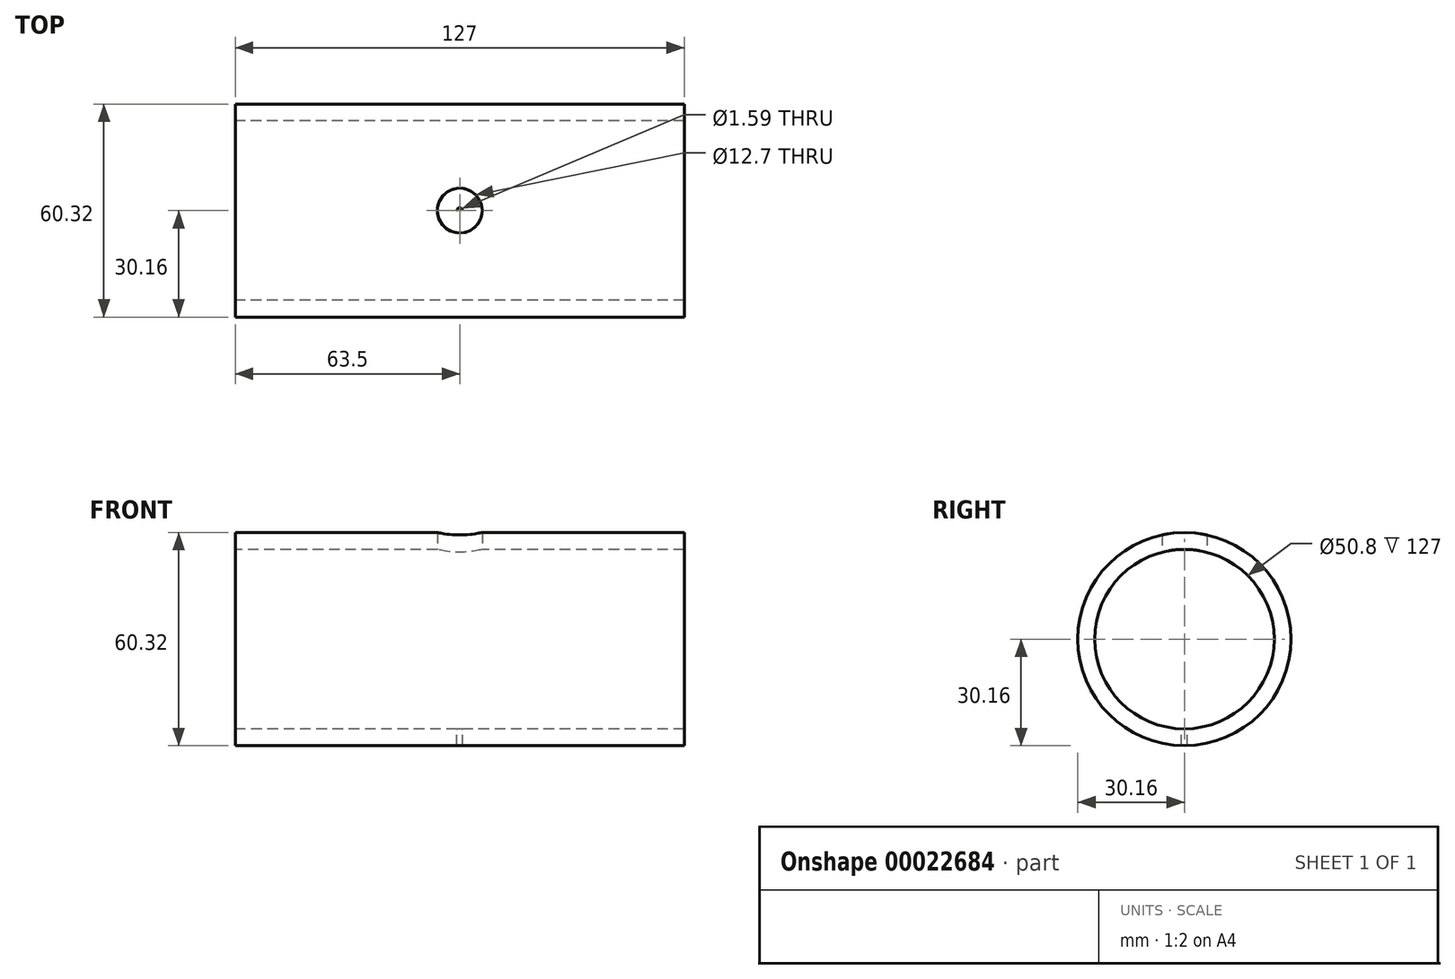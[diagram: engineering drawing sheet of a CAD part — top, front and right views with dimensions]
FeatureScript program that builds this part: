
annotation { "Feature Type Name" : "Feature", "Feature Type Description" : "" }
export const myFeature = defineFeature(function(context is Context, id is Id, definition is map)
    precondition{}
    {
        {
            var Q0;
            Q0=qCreatedBy(makeId("Right.planeOp"),FACE);
            var sketch = newSketch(context, id + "F0", { "sketchPlane" : qUnion([Q0])});
            skCircle(sketch, "E0", {"center": v(0, 0) * mm, "radius": 25.4 * mm});
            skCircle(sketch, "E1", {"center": v(0, 0) * mm, "radius": 30.16 * mm});
            skSolve(sketch);
        }
        {
            var Q0;
            Q0=qSketchRegion(id+"F0",true);
            extrude(context, id + "F1", {"entities" : qUnion([Q0]), "depth" : 127 * mm});
        }
        {
            var Q0;
            Q0=qCreatedBy(makeId("Top.planeOp"),FACE);
            var sketch = newSketch(context, id + "F2", { "sketchPlane" : qUnion([Q0])});
            skPoint(sketch, "E2", {"position": v(63.5, 0) * mm});
            skSolve(sketch);
        }
        {
            var Q0;
            Q0=sQuery(id+"F2.wireOp",VERTEX,"E2");
            var Q1;
            Q1=makeQuery(id+"F1.opExtrude","SWEPT_BODY",BODY,{"disambiguationData":[OSD([sQuery(id+"F0.wireOp",EDGE,"E0"),sQuery(id+"F0.wireOp",EDGE,"E1")])]});
            hole(context, id + "F3", {"style" : HoleStyle.SIMPLE, "holeDiameter" : 1.59 * mm, "endStyle" : HoleEndStyle.THROUGH, "locations" : qUnion([Q0]), "scope" : qUnion([Q1])});
        }
        {
            var Q0;
            Q0=qCreatedBy(makeId("Top.planeOp"),FACE);
            var sketch = newSketch(context, id + "F4", { "sketchPlane" : qUnion([Q0])});
            skPoint(sketch, "E3", {"position": v(63.5, 0) * mm});
            skSolve(sketch);
        }
        {
            var Q0;
            Q0=sQuery(id+"F4.wireOp",VERTEX,"E3");
            var Q1;
            Q1=makeQuery(id+"F1.opExtrude","SWEPT_BODY",BODY,{"disambiguationData":[OSD([sQuery(id+"F0.wireOp",EDGE,"E0"),sQuery(id+"F0.wireOp",EDGE,"E1")])]});
            hole(context, id + "F5", {"style" : HoleStyle.SIMPLE, "holeDiameter" : 12.7 * mm, "endStyle" : HoleEndStyle.THROUGH, "oppositeDirection" : true, "locations" : qUnion([Q0]), "scope" : qUnion([Q1])});
        }
    });
